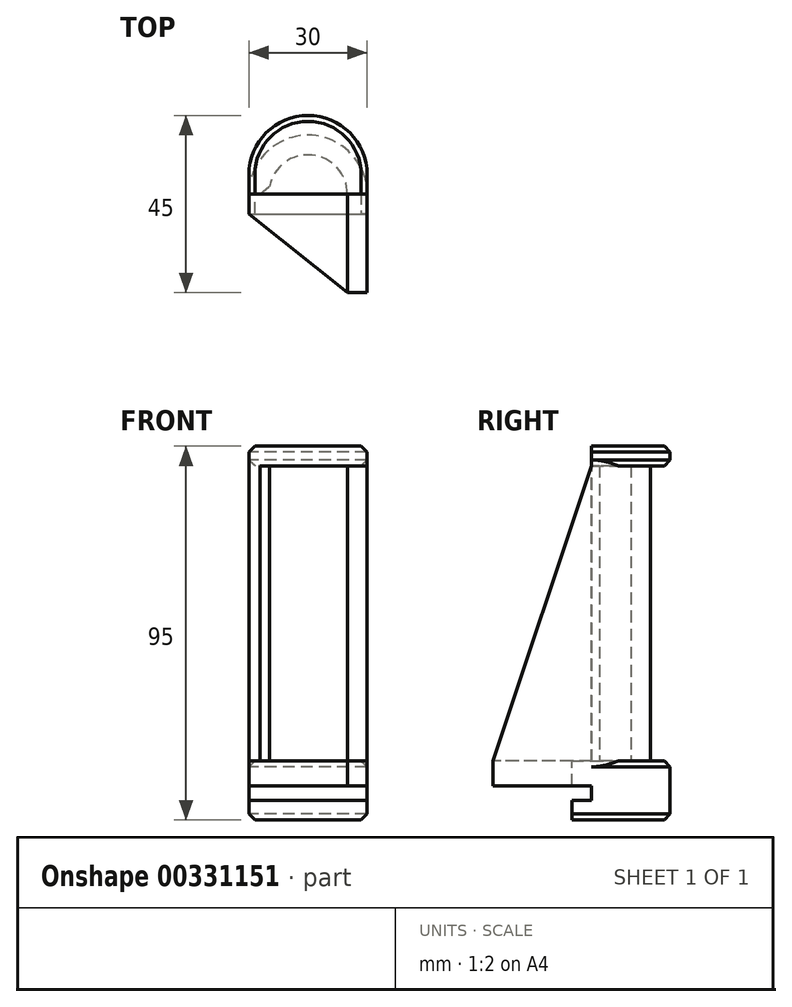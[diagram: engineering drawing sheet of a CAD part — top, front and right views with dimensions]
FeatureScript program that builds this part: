
annotation { "Feature Type Name" : "Feature", "Feature Type Description" : "" }
export const myFeature = defineFeature(function(context is Context, id is Id, definition is map)
    precondition{}
    {
        {
            var Q0;
            Q0=qCreatedBy(makeId("Top.planeOp"),FACE);
            var sketch = newSketch(context, id + "F0", { "sketchPlane" : qUnion([Q0])});
            skLineSegment(sketch, "E0.bottom", {"start": v(0, 0) * mm, "end": v(30, 0) * mm});
            skLineSegment(sketch, "E0.left", {"start": v(0, 0) * mm, "end": v(0, 5) * mm});
            skLineSegment(sketch, "E0.right", {"start": v(30, 0) * mm, "end": v(30, 5) * mm});
            skArc(sketch, "E1", {"start": v(30, 5) * mm, "mid": v(15, 20) * mm, "end": v(0, 5) * mm});
            skSolve(sketch);
        }
        {
            var Q0;
            Q0=makeQuery(id+"F0.imprint","IMPRINT",FACE,{"disambiguationData":[TD([[makeQuery(id+"F0.imprint","IMPRINT",EDGE,{"derivedFrom":sQuery(id+"F0.wireOp",EDGE,"E0.bottom")}),1.0]])]});
            extrude(context, id + "F1", {"entities" : qUnion([Q0]), "depth" : 15 * mm});
        }
        {
            var Q0;
            Q0=makeQuery(id+"F1.opExtrude","SWEPT_FACE",FACE,{"disambiguationData":[OSD([sQuery(id+"F0.wireOp",EDGE,"E0.bottom")])]});
            var sketch = newSketch(context, id + "F2", { "sketchPlane" : qUnion([Q0])});
            skLineSegment(sketch, "E2.bottom", {"start": v(0, 0) * mm, "end": v(30, 0) * mm});
            skLineSegment(sketch, "E2.top", {"start": v(0, 5) * mm, "end": v(30, 5) * mm});
            skLineSegment(sketch, "E2.left", {"start": v(0, 0) * mm, "end": v(0, 5) * mm});
            skLineSegment(sketch, "E2.right", {"start": v(30, 0) * mm, "end": v(30, 5) * mm});
            skSolve(sketch);
        }
        {
            var Q0;
            Q0=makeQuery(id+"F2.imprint","IMPRINT",FACE,{"disambiguationData":[TD([[makeQuery(id+"F2.imprint","IMPRINT",EDGE,{"derivedFrom":sQuery(id+"F2.wireOp",EDGE,"E2.bottom")}),1.0]])]});
            extrude(context, id + "F3", {"entities" : qUnion([Q0]), "operationType" : NewBodyOperationType.ADD, "depth" : 5 * mm});
        }
        {
            var Q0;
            Q0=makeQuery(id+"F1.opExtrude","SWEPT_FACE",FACE,{"disambiguationData":[OSD([sQuery(id+"F0.wireOp",EDGE,"E0.bottom")])]});
            var sketch = newSketch(context, id + "F4", { "sketchPlane" : qUnion([Q0])});
            skLineSegment(sketch, "E3.bottom", {"start": v(0, 15) * mm, "end": v(30, 15) * mm});
            skLineSegment(sketch, "E3.top", {"start": v(0, 8.7) * mm, "end": v(30, 8.7) * mm});
            skLineSegment(sketch, "E3.left", {"start": v(0, 15) * mm, "end": v(0, 8.7) * mm});
            skLineSegment(sketch, "E3.right", {"start": v(30, 15) * mm, "end": v(30, 8.7) * mm});
            skSolve(sketch);
        }
        {
            var Q0;
            Q0=makeQuery(id+"F4.imprint","IMPRINT",FACE,{"disambiguationData":[TD([[makeQuery(id+"F4.imprint","IMPRINT",EDGE,{"derivedFrom":sQuery(id+"F4.wireOp",EDGE,"E3.bottom")}),-1.0]])]});
            extrude(context, id + "F5", {"entities" : qUnion([Q0]), "operationType" : NewBodyOperationType.ADD, "depth" : 25 * mm});
        }
        {
            var Q0;
            Q0=makeQuery(id+"F5.boolean.opBoolean","MERGE",FACE,{"derivedFrom":[makeQuery(id+"F1.opExtrude","CAP_FACE",FACE,{"disambiguationData":[OSD([sQuery(id+"F0.wireOp",EDGE,"E0.bottom"),sQuery(id+"F0.wireOp",EDGE,"E0.left"),sQuery(id+"F0.wireOp",EDGE,"E0.right"),sQuery(id+"F0.wireOp",EDGE,"E1")])],"isStart":false}),makeQuery(id+"F5.opExtrude","SWEPT_FACE",FACE,{"disambiguationData":[OSD([sQuery(id+"F4.wireOp",EDGE,"E3.bottom")])]})]});
            var sketch = newSketch(context, id + "F6", { "sketchPlane" : qUnion([Q0])});
            skArc(sketch, "E4", {"start": v(30, 0) * mm, "mid": v(15, 15) * mm, "end": v(0, 0) * mm});
            skArc(sketch, "E5", {"start": v(25, 0) * mm, "mid": v(15, 10) * mm, "end": v(5, 0) * mm});
            skLineSegment(sketch, "E6", {"start": v(5, 0) * mm, "end": v(0, 0) * mm});
            skLineSegment(sketch, "E7.top", {"start": v(25, -25) * mm, "end": v(30, -25) * mm});
            skLineSegment(sketch, "E7.left", {"start": v(25, 0) * mm, "end": v(25, -25) * mm});
            skLineSegment(sketch, "E7.right", {"start": v(30, 0) * mm, "end": v(30, -25) * mm});
            skSolve(sketch);
        }
        {
            var Q0;
            Q0=makeQuery(id+"F6.imprint","IMPRINT",FACE,{"disambiguationData":[TD([[makeQuery(id+"F6.imprint","IMPRINT",EDGE,{"derivedFrom":sQuery(id+"F6.wireOp",EDGE,"E4")}),1.0]])]});
            extrude(context, id + "F7", {"entities" : qUnion([Q0]), "operationType" : NewBodyOperationType.ADD, "depth" : 75 * mm});
        }
        {
            var Q0;
            Q0=makeQuery(id+"F7.opExtrude","SWEPT_FACE",FACE,{"disambiguationData":[OSD([sQuery(id+"F6.wireOp",EDGE,"E7.left")])]});
            var sketch = newSketch(context, id + "F8", { "sketchPlane" : qUnion([Q0])});
            skLineSegment(sketch, "E8", {"start": v(0, 90) * mm, "end": v(25, 90) * mm});
            skLineSegment(sketch, "E9", {"start": v(25, 90) * mm, "end": v(25, 15) * mm});
            skLineSegment(sketch, "E10", {"start": v(25, 15) * mm, "end": v(0, 90) * mm});
            skSolve(sketch);
        }
        {
            var Q0;
            Q0=makeQuery(id+"F8.imprint","IMPRINT",FACE,{"disambiguationData":[TD([[makeQuery(id+"F8.imprint","IMPRINT",EDGE,{"derivedFrom":sQuery(id+"F8.wireOp",EDGE,"E8")}),-1.0]])]});
            extrude(context, id + "F9", {"entities" : qUnion([Q0]), "operationType" : NewBodyOperationType.REMOVE, "endBound" : BoundingType.THROUGH_ALL, "oppositeDirection" : true, "depth" : 25 * mm});
        }
        {
            var Q0;
            Q0=makeQuery(id+"F7.opExtrude","CAP_FACE",FACE,{"disambiguationData":[OSD([sQuery(id+"F6.wireOp",EDGE,"E4"),sQuery(id+"F6.wireOp",EDGE,"E5"),sQuery(id+"F6.wireOp",EDGE,"E6"),sQuery(id+"F6.wireOp",EDGE,"E7.top"),sQuery(id+"F6.wireOp",EDGE,"E7.left"),sQuery(id+"F6.wireOp",EDGE,"E7.right")])],"isStart":false});
            var sketch = newSketch(context, id + "F10", { "sketchPlane" : qUnion([Q0])});
            skArc(sketch, "E11.0", {"start": v(30, 5) * mm, "mid": v(15, 20) * mm, "end": v(0, 5) * mm});
            skLineSegment(sketch, "E12.0", {"start": v(0, 0) * mm, "end": v(0, 5) * mm});
            skLineSegment(sketch, "E13", {"start": v(30, 5) * mm, "end": v(30, 0) * mm});
            skLineSegment(sketch, "E14", {"start": v(30, 0) * mm, "end": v(0, 0) * mm});
            skSolve(sketch);
        }
        {
            var Q0;
            Q0 = qSketchRegion(id + "F10", true);
            extrude(context, id + "F11", {"entities" : qUnion([Q0]), "operationType" : NewBodyOperationType.ADD, "depth" : 5 * mm});
        }
        {
            var Q0;
            {var subQ1=sQuery(id+"F4.wireOp",EDGE,"E3.bottom");var subQ2=sQuery(id+"F0.wireOp",EDGE,"E0.left");var subQ3=makeQuery(id+"F1.opExtrude","CAP_FACE",FACE,{"disambiguationData":[OSD([sQuery(id+"F0.wireOp",EDGE,"E0.bottom"),subQ2,sQuery(id+"F0.wireOp",EDGE,"E0.right"),sQuery(id+"F0.wireOp",EDGE,"E1")])],"isStart":false});var subQ4=makeQuery(id+"F5.opExtrude","SWEPT_FACE",FACE,{"disambiguationData":[OSD([subQ1])]});Q0=makeQuery(id+"F7.boolean.opBoolean","SPLIT",FACE,{"disambiguationData":[TD([makeQuery(id+"F7.opExtrude","SWEPT_FACE",FACE,{"disambiguationData":[OSD([sQuery(id+"F6.wireOp",EDGE,"E5")])]})])],"derivedFrom":makeQuery(id+"F5.boolean.opBoolean","MERGE",FACE,{"derivedFrom":[subQ3,subQ4]})});}
            var sketch = newSketch(context, id + "F12", { "sketchPlane" : qUnion([Q0])});
            skLineSegment(sketch, "E15.0.0", {"start": v(0, 5) * mm, "end": v(0, -5) * mm, "construction": true});
            skLineSegment(sketch, "E15.0.2", {"start": v(0, -5) * mm, "end": v(0, 0) * mm, "construction": true});
            skLineSegment(sketch, "E15.0.4", {"start": v(0, 0) * mm, "end": v(0, -25) * mm, "construction": true});
            skLineSegment(sketch, "E15.0.6", {"start": v(0, -25) * mm, "end": v(0, 0) * mm, "construction": true});
            skLineSegment(sketch, "E15.0.7", {"start": v(0, 0) * mm, "end": v(0, 5) * mm, "construction": true});
            skLineSegment(sketch, "E16.0.0", {"start": v(30, -5) * mm, "end": v(0, -5) * mm, "construction": true});
            skLineSegment(sketch, "E16.0.2", {"start": v(0, -5) * mm, "end": v(30, -5) * mm, "construction": true});
            skLineSegment(sketch, "E17.0", {"start": v(0, 0) * mm, "end": v(30, 0) * mm, "construction": true});
            skLineSegment(sketch, "E18", {"start": v(0, -5) * mm, "end": v(25, -25) * mm});
            skLineSegment(sketch, "E19", {"start": v(25, -25) * mm, "end": v(0, -25) * mm});
            skSolve(sketch);
        }
        {
            var Q0;
            {var subQ0=sQuery(id+"F12.wireOp",EDGE,"E18");Q0=makeQuery(id+"F12.imprint","IMPRINT",FACE,{"disambiguationData":[TD([[makeQuery(id+"F12.imprint","IMPRINT",EDGE,{"derivedFrom":subQ0}),-1.0]])]});}
            extrude(context, id + "F13", {"entities" : qUnion([Q0]), "operationType" : NewBodyOperationType.REMOVE, "endBound" : BoundingType.THROUGH_ALL, "oppositeDirection" : true, "depth" : 25 * mm});
        }
        {
            var Q0;
            Q0=makeQuery(id+"F7.opExtrude","SWEPT_EDGE",EDGE,{"disambiguationData":[OSD([sQuery(id+"F6.wireOp",EDGE,"E5"),sQuery(id+"F6.wireOp",EDGE,"E6")])]});
            chamfer(context, id + "F14", {"entities" : qUnion([Q0]), "width" : 2.5 * mm, "tangentPropagation" : true});
        }
        {
            var Q0;
            Q0=makeQuery(id+"F11.opExtrude","CAP_EDGE",EDGE,{"disambiguationData":[OSD([sQuery(id+"F10.wireOp",EDGE,"E11.0")])],"isStart":true});
            var Q1;
            Q1=makeQuery(id+"F11.opExtrude","CAP_EDGE",EDGE,{"disambiguationData":[OSD([sQuery(id+"F10.wireOp",EDGE,"E11.0")])],"isStart":false});
            var Q2;
            Q2=makeQuery(id+"F1.opExtrude","CAP_EDGE",EDGE,{"disambiguationData":[OSD([sQuery(id+"F0.wireOp",EDGE,"E1")])],"isStart":false});
            var Q3;
            Q3=makeQuery(id+"F1.opExtrude","CAP_EDGE",EDGE,{"disambiguationData":[OSD([sQuery(id+"F0.wireOp",EDGE,"E1")])],"isStart":true});
            chamfer(context, id + "F15", {"entities" : qUnion([Q0, Q1, Q2, Q3]), "width" : 1.5 * mm, "tangentPropagation" : true});
        }
    });
